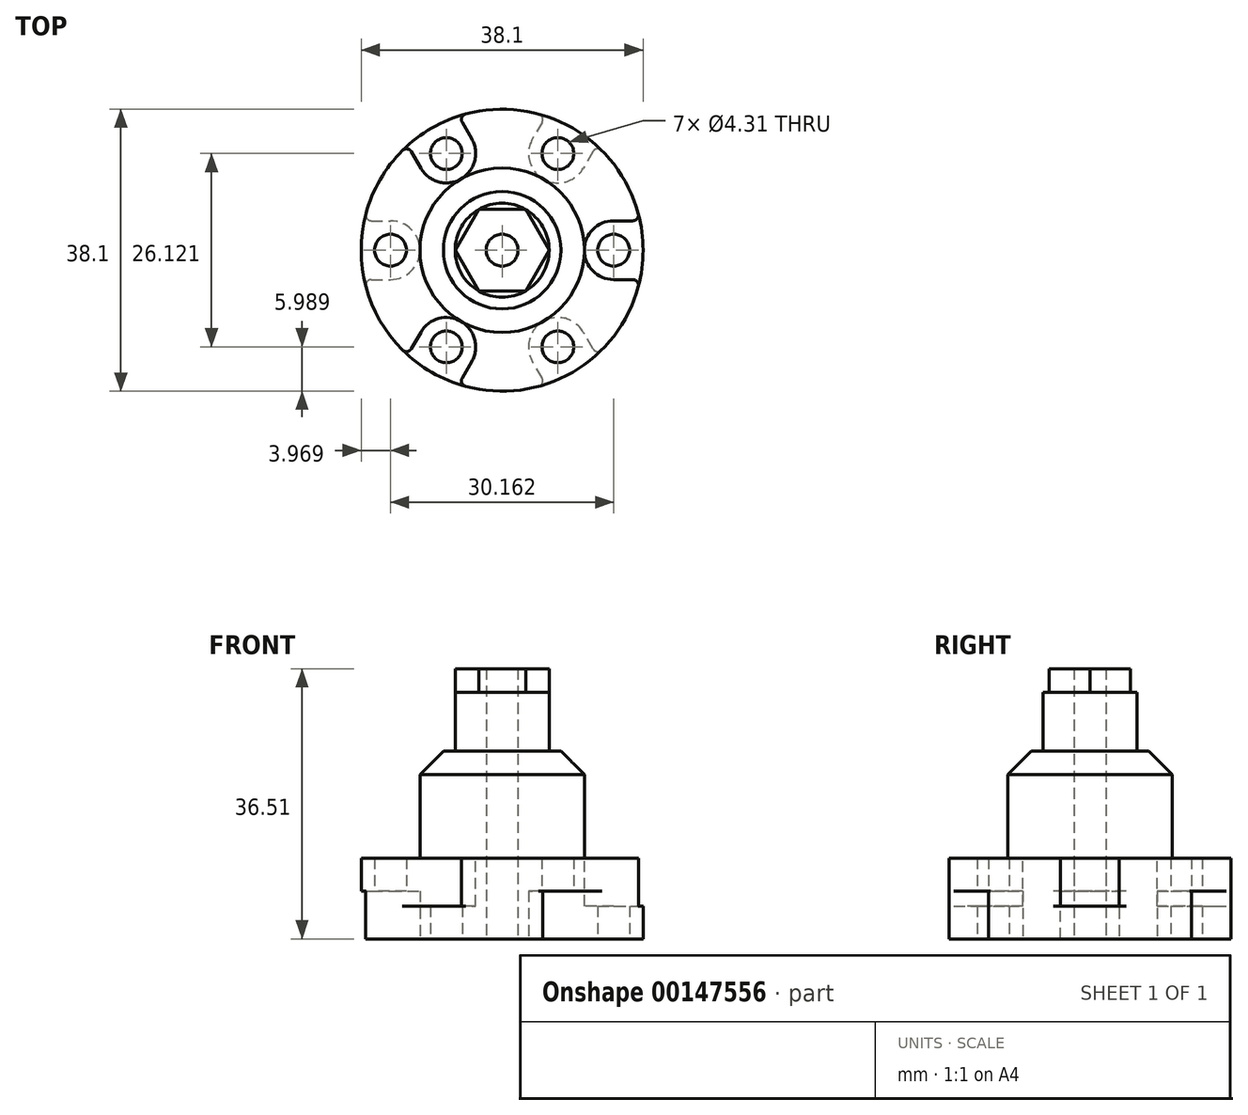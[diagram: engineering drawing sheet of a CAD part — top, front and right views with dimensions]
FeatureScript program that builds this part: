
annotation { "Feature Type Name" : "Feature", "Feature Type Description" : "" }
export const myFeature = defineFeature(function(context is Context, id is Id, definition is map)
    precondition{}
    {
        {
            var Q0;
            Q0=qCreatedBy(makeId("Top.planeOp"),FACE);
            var sketch = newSketch(context, id + "F0", { "sketchPlane" : qUnion([Q0])});
            skCircle(sketch, "E0", {"center": v(0, 0) * mm, "radius": 19.05 * mm});
            skCircle(sketch, "E1", {"center": v(7.54, -13.06) * mm, "radius": 3.97 * mm, "construction": true});
            skCircle(sketch, "E2", {"center": v(0, 0) * mm, "radius": 11.11 * mm, "construction": true});
            skCircle(sketch, "E3.cCircle", {"center": v(0, 0) * mm, "radius": 13.06 * mm, "construction": true});
            skLineSegment(sketch, "E3.0", {"start": v(-7.54, 13.06) * mm, "end": v(7.54, 13.06) * mm, "construction": true});
            skLineSegment(sketch, "E3.1", {"start": v(7.54, 13.06) * mm, "end": v(15.08, 0) * mm, "construction": true});
            skLineSegment(sketch, "E3.2", {"start": v(15.08, 0) * mm, "end": v(7.54, -13.06) * mm, "construction": true});
            skLineSegment(sketch, "E3.3", {"start": v(7.54, -13.06) * mm, "end": v(-7.54, -13.06) * mm, "construction": true});
            skLineSegment(sketch, "E3.4", {"start": v(-7.54, -13.06) * mm, "end": v(-15.08, 0) * mm, "construction": true});
            skLineSegment(sketch, "E3.5", {"start": v(-15.08, 0) * mm, "end": v(-7.54, 13.06) * mm, "construction": true});
            skPoint(sketch, "E3.0.midPoint", {"position": v(0, 13.06) * mm});
            skCircle(sketch, "E4", {"center": v(-7.54, -13.06) * mm, "radius": 2.15 * mm});
            skCircle(sketch, "E5", {"center": v(-15.08, 0) * mm, "radius": 2.15 * mm});
            skCircle(sketch, "E6", {"center": v(-7.54, 13.06) * mm, "radius": 2.15 * mm});
            skCircle(sketch, "E7", {"center": v(7.54, 13.06) * mm, "radius": 2.15 * mm});
            skCircle(sketch, "E8", {"center": v(15.08, 0) * mm, "radius": 2.15 * mm});
            skCircle(sketch, "E9", {"center": v(7.54, -13.06) * mm, "radius": 2.15 * mm});
            skCircle(sketch, "E10", {"center": v(0, 0) * mm, "radius": 2.15 * mm});
            skSolve(sketch);
        }
        {
            var Q0;
            Q0=qSketchRegion(id+"F0",true);
            extrude(context, id + "F1", {"entities" : qUnion([Q0]), "depth" : 10.92 * mm});
        }
        {
            var Q0;
            Q0=makeQuery(id+"F1.opExtrude","CAP_FACE",FACE,{"disambiguationData":[OSD([sQuery(id+"F0.wireOp",EDGE,"E0"),sQuery(id+"F0.wireOp",EDGE,"E4"),sQuery(id+"F0.wireOp",EDGE,"E5"),sQuery(id+"F0.wireOp",EDGE,"E6"),sQuery(id+"F0.wireOp",EDGE,"E7"),sQuery(id+"F0.wireOp",EDGE,"E8"),sQuery(id+"F0.wireOp",EDGE,"E9")])],"isStart":false});
            cPlane(context, id + "F2", {"entities" : qUnion([Q0]), "cplaneType" : CPlaneType.OFFSET, "offset" : 4.44 * mm, "oppositeDirection" : true, "width" : 152.4 * mm, "height" : 152.4 * mm});
        }
        {
            var Q0;
            Q0=makeQuery(id+"F1.opExtrude","CAP_FACE",FACE,{"disambiguationData":[OSD([sQuery(id+"F0.wireOp",EDGE,"E0"),sQuery(id+"F0.wireOp",EDGE,"E4"),sQuery(id+"F0.wireOp",EDGE,"E5"),sQuery(id+"F0.wireOp",EDGE,"E6"),sQuery(id+"F0.wireOp",EDGE,"E7"),sQuery(id+"F0.wireOp",EDGE,"E8"),sQuery(id+"F0.wireOp",EDGE,"E9")])],"isStart":true});
            cPlane(context, id + "F3", {"entities" : qUnion([Q0]), "cplaneType" : CPlaneType.OFFSET, "offset" : 4.44 * mm, "oppositeDirection" : true, "width" : 152.4 * mm, "height" : 152.4 * mm});
        }
        {
            var Q0;
            Q0=makeQuery(id+"F1.opExtrude","CAP_FACE",FACE,{"disambiguationData":[OSD([sQuery(id+"F0.wireOp",EDGE,"E0"),sQuery(id+"F0.wireOp",EDGE,"E4"),sQuery(id+"F0.wireOp",EDGE,"E5"),sQuery(id+"F0.wireOp",EDGE,"E6"),sQuery(id+"F0.wireOp",EDGE,"E7"),sQuery(id+"F0.wireOp",EDGE,"E8"),sQuery(id+"F0.wireOp",EDGE,"E9")])],"isStart":false});
            var sketch = newSketch(context, id + "F4", { "sketchPlane" : qUnion([Q0])});
            skLineSegment(sketch, "E11", {"start": v(-7.54, 13.06) * mm, "end": v(0, 0) * mm, "construction": true});
            skLineSegment(sketch, "E12", {"start": v(15.08, 0) * mm, "end": v(0, 0) * mm, "construction": true});
            skLineSegment(sketch, "E13", {"start": v(0, 0) * mm, "end": v(-7.54, -13.06) * mm, "construction": true});
            skLineSegment(sketch, "E14.bottom", {"start": v(-10.98, 11.08) * mm, "end": v(-4.1, 15.05) * mm, "construction": true});
            skLineSegment(sketch, "E14.top", {"start": v(-12.96, 14.51) * mm, "end": v(-6.09, 18.48) * mm});
            skLineSegment(sketch, "E14.left", {"start": v(-10.98, 11.08) * mm, "end": v(-12.96, 14.51) * mm});
            skLineSegment(sketch, "E14.right", {"start": v(-4.1, 15.05) * mm, "end": v(-6.09, 18.48) * mm});
            skLineSegment(sketch, "E15.bottom", {"start": v(15.08, 3.97) * mm, "end": v(19.05, 3.97) * mm});
            skLineSegment(sketch, "E15.top", {"start": v(15.08, -3.97) * mm, "end": v(19.05, -3.97) * mm});
            skLineSegment(sketch, "E15.left", {"start": v(15.08, 3.97) * mm, "end": v(15.08, -3.97) * mm, "construction": true});
            skLineSegment(sketch, "E15.right", {"start": v(19.05, 3.97) * mm, "end": v(19.05, -3.97) * mm});
            skLineSegment(sketch, "E16.bottom", {"start": v(-10.98, -11.08) * mm, "end": v(-4.1, -15.05) * mm, "construction": true});
            skLineSegment(sketch, "E16.top", {"start": v(-12.96, -14.51) * mm, "end": v(-6.09, -18.48) * mm});
            skLineSegment(sketch, "E16.left", {"start": v(-10.98, -11.08) * mm, "end": v(-12.96, -14.51) * mm});
            skLineSegment(sketch, "E16.right", {"start": v(-4.1, -15.05) * mm, "end": v(-6.09, -18.48) * mm});
            skArc(sketch, "E17", {"start": v(-4.1, -15.05) * mm, "mid": v(-5.56, -9.62) * mm, "end": v(-10.98, -11.08) * mm});
            skArc(sketch, "E18", {"start": v(15.08, 3.97) * mm, "mid": v(11.11, 0) * mm, "end": v(15.08, -3.97) * mm});
            skArc(sketch, "E19", {"start": v(-10.98, 11.08) * mm, "mid": v(-5.56, 9.62) * mm, "end": v(-4.1, 15.05) * mm});
            skSolve(sketch);
        }
        {
            var Q0;
            Q0=qSketchRegion(id+"F4",true);
            var Q1;
            Q1=qCreatedBy(id+"F3.planeOp",FACE);
            extrude(context, id + "F5", {"entities" : qUnion([Q0]), "operationType" : NewBodyOperationType.REMOVE, "endBound" : BoundingType.UP_TO_SURFACE, "oppositeDirection" : true, "endBoundEntityFace" : qUnion([Q1]), "depth" : 25.4 * mm});
        }
        {
            var Q0;
            Q0=makeQuery(id+"F1.opExtrude","CAP_FACE",FACE,{"disambiguationData":[OSD([sQuery(id+"F0.wireOp",EDGE,"E0"),sQuery(id+"F0.wireOp",EDGE,"E4"),sQuery(id+"F0.wireOp",EDGE,"E5"),sQuery(id+"F0.wireOp",EDGE,"E6"),sQuery(id+"F0.wireOp",EDGE,"E7"),sQuery(id+"F0.wireOp",EDGE,"E8"),sQuery(id+"F0.wireOp",EDGE,"E9"),sQuery(id+"F0.wireOp",EDGE,"E10")])],"isStart":true});
            var sketch = newSketch(context, id + "F6", { "sketchPlane" : qUnion([Q0])});
            skLineSegment(sketch, "E20", {"start": v(0, 0) * mm, "end": v(-15.08, 0) * mm, "construction": true});
            skLineSegment(sketch, "E21", {"start": v(0, 0) * mm, "end": v(7.54, 13.06) * mm, "construction": true});
            skLineSegment(sketch, "E22", {"start": v(0, 0) * mm, "end": v(7.54, -13.06) * mm, "construction": true});
            skLineSegment(sketch, "E23.bottom", {"start": v(6.09, -18.48) * mm, "end": v(12.96, -14.51) * mm});
            skLineSegment(sketch, "E23.top", {"start": v(4.1, -15.05) * mm, "end": v(10.98, -11.08) * mm, "construction": true});
            skLineSegment(sketch, "E23.left", {"start": v(6.09, -18.48) * mm, "end": v(4.1, -15.05) * mm});
            skLineSegment(sketch, "E23.right", {"start": v(12.96, -14.51) * mm, "end": v(10.98, -11.08) * mm});
            skLineSegment(sketch, "E24.bottom", {"start": v(6.09, 18.48) * mm, "end": v(12.96, 14.51) * mm});
            skLineSegment(sketch, "E24.top", {"start": v(4.1, 15.05) * mm, "end": v(10.98, 11.08) * mm, "construction": true});
            skLineSegment(sketch, "E24.left", {"start": v(6.09, 18.48) * mm, "end": v(4.1, 15.05) * mm});
            skLineSegment(sketch, "E24.right", {"start": v(12.96, 14.51) * mm, "end": v(10.98, 11.08) * mm});
            skLineSegment(sketch, "E25.bottom", {"start": v(-19.05, 3.97) * mm, "end": v(-15.08, 3.97) * mm});
            skLineSegment(sketch, "E25.top", {"start": v(-19.05, -3.97) * mm, "end": v(-15.08, -3.97) * mm});
            skLineSegment(sketch, "E25.left", {"start": v(-19.05, 3.97) * mm, "end": v(-19.05, -3.97) * mm});
            skLineSegment(sketch, "E25.right", {"start": v(-15.08, 3.97) * mm, "end": v(-15.08, -3.97) * mm, "construction": true});
            skArc(sketch, "E26", {"start": v(10.98, -11.08) * mm, "mid": v(5.56, -9.62) * mm, "end": v(4.1, -15.05) * mm});
            skArc(sketch, "E27", {"start": v(4.1, 15.05) * mm, "mid": v(5.56, 9.62) * mm, "end": v(10.98, 11.08) * mm});
            skArc(sketch, "E28", {"start": v(-15.08, -3.97) * mm, "mid": v(-11.11, 0) * mm, "end": v(-15.08, 3.97) * mm});
            skSolve(sketch);
        }
        {
            var Q0;
            Q0=qSketchRegion(id+"F6",true);
            var Q1;
            Q1=qCreatedBy(id+"F2.planeOp",FACE);
            extrude(context, id + "F7", {"entities" : qUnion([Q0]), "operationType" : NewBodyOperationType.REMOVE, "endBound" : BoundingType.UP_TO_SURFACE, "oppositeDirection" : true, "endBoundEntityFace" : qUnion([Q1]), "depth" : 25.4 * mm});
        }
        {
            var Q0;
            Q0=makeQuery(id+"F1.opExtrude","CAP_FACE",FACE,{"disambiguationData":[OSD([sQuery(id+"F0.wireOp",EDGE,"E0"),sQuery(id+"F0.wireOp",EDGE,"E4"),sQuery(id+"F0.wireOp",EDGE,"E5"),sQuery(id+"F0.wireOp",EDGE,"E6"),sQuery(id+"F0.wireOp",EDGE,"E7"),sQuery(id+"F0.wireOp",EDGE,"E8"),sQuery(id+"F0.wireOp",EDGE,"E9"),sQuery(id+"F0.wireOp",EDGE,"E10")])],"isStart":false});
            var sketch = newSketch(context, id + "F8", { "sketchPlane" : qUnion([Q0])});
            skCircle(sketch, "E29", {"center": v(0, 0) * mm, "radius": 11.11 * mm});
            skCircle(sketch, "E30", {"center": v(0, 0) * mm, "radius": 2.15 * mm});
            skSolve(sketch);
        }
        {
            var Q0;
            Q0=qSketchRegion(id+"F8",true);
            extrude(context, id + "F9", {"entities" : qUnion([Q0]), "operationType" : NewBodyOperationType.ADD, "depth" : 14.48 * mm});
        }
        {
            var Q0;
            Q0=makeQuery(id+"F9.opExtrude","CAP_FACE",FACE,{"disambiguationData":[OSD([sQuery(id+"F8.wireOp",EDGE,"E29"),sQuery(id+"F8.wireOp",EDGE,"E30")])],"isStart":false});
            var sketch = newSketch(context, id + "F10", { "sketchPlane" : qUnion([Q0])});
            skCircle(sketch, "E31", {"center": v(0, 0) * mm, "radius": 6.35 * mm});
            skCircle(sketch, "E32", {"center": v(0, 0) * mm, "radius": 2.15 * mm});
            skSolve(sketch);
        }
        {
            var Q0;
            Q0=qSketchRegion(id+"F10",true);
            extrude(context, id + "F11", {"entities" : qUnion([Q0]), "operationType" : NewBodyOperationType.ADD, "depth" : 7.94 * mm});
        }
        {
            var Q0;
            Q0=makeQuery(id+"F11.opExtrude","CAP_FACE",FACE,{"disambiguationData":[OSD([sQuery(id+"F10.wireOp",EDGE,"E31"),sQuery(id+"F10.wireOp",EDGE,"E32")])],"isStart":false});
            var sketch = newSketch(context, id + "F12", { "sketchPlane" : qUnion([Q0])});
            skCircle(sketch, "E33.cCircle", {"center": v(0, 0) * mm, "radius": 6.35 * mm, "construction": true});
            skLineSegment(sketch, "E33.0", {"start": v(-3.18, 5.5) * mm, "end": v(3.17, 5.5) * mm});
            skLineSegment(sketch, "E33.1", {"start": v(3.17, 5.5) * mm, "end": v(6.35, 0) * mm});
            skLineSegment(sketch, "E33.2", {"start": v(6.35, 0) * mm, "end": v(3.18, -5.5) * mm});
            skLineSegment(sketch, "E33.3", {"start": v(3.18, -5.5) * mm, "end": v(-3.17, -5.5) * mm});
            skLineSegment(sketch, "E33.4", {"start": v(-3.17, -5.5) * mm, "end": v(-6.35, 0) * mm});
            skLineSegment(sketch, "E33.5", {"start": v(-6.35, 0) * mm, "end": v(-3.18, 5.5) * mm});
            skCircle(sketch, "E34", {"center": v(0, 0) * mm, "radius": 2.15 * mm});
            skSolve(sketch);
        }
        {
            var Q0;
            Q0=qSketchRegion(id+"F12",true);
            extrude(context, id + "F13", {"entities" : qUnion([Q0]), "operationType" : NewBodyOperationType.ADD, "depth" : 3.17 * mm});
        }
        {
            var Q0;
            Q0=makeQuery(id+"F5.boolean.opBoolean","INTERSECT",EDGE,{"derivedFrom":[makeQuery(id+"F1.opExtrude","SWEPT_FACE",FACE,{"disambiguationData":[OSD([sQuery(id+"F0.wireOp",EDGE,"E0")])]}),makeQuery(id+"F5.opExtrude","SWEPT_FACE",FACE,{"disambiguationData":[OSD([sQuery(id+"F4.wireOp",EDGE,"E16.left")])]})]});
            var Q1;
            Q1=makeQuery(id+"F7.boolean.opBoolean","INTERSECT",EDGE,{"derivedFrom":[makeQuery(id+"F1.opExtrude","SWEPT_FACE",FACE,{"disambiguationData":[OSD([sQuery(id+"F0.wireOp",EDGE,"E0")])]}),makeQuery(id+"F7.opExtrude","SWEPT_FACE",FACE,{"disambiguationData":[OSD([sQuery(id+"F6.wireOp",EDGE,"E24.left")])]})]});
            var Q2;
            Q2=makeQuery(id+"F7.boolean.opBoolean","INTERSECT",EDGE,{"derivedFrom":[makeQuery(id+"F1.opExtrude","SWEPT_FACE",FACE,{"disambiguationData":[OSD([sQuery(id+"F0.wireOp",EDGE,"E0")])]}),makeQuery(id+"F7.opExtrude","SWEPT_FACE",FACE,{"disambiguationData":[OSD([sQuery(id+"F6.wireOp",EDGE,"E24.right")])]})]});
            var Q3;
            Q3=makeQuery(id+"F5.boolean.opBoolean","INTERSECT",EDGE,{"derivedFrom":[makeQuery(id+"F1.opExtrude","SWEPT_FACE",FACE,{"disambiguationData":[OSD([sQuery(id+"F0.wireOp",EDGE,"E0")])]}),makeQuery(id+"F5.opExtrude","SWEPT_FACE",FACE,{"disambiguationData":[OSD([sQuery(id+"F4.wireOp",EDGE,"E15.bottom")])]})]});
            var Q4;
            Q4=makeQuery(id+"F5.boolean.opBoolean","INTERSECT",EDGE,{"derivedFrom":[makeQuery(id+"F1.opExtrude","SWEPT_FACE",FACE,{"disambiguationData":[OSD([sQuery(id+"F0.wireOp",EDGE,"E0")])]}),makeQuery(id+"F5.opExtrude","SWEPT_FACE",FACE,{"disambiguationData":[OSD([sQuery(id+"F4.wireOp",EDGE,"E15.top")])]})]});
            var Q5;
            Q5=makeQuery(id+"F5.boolean.opBoolean","INTERSECT",EDGE,{"derivedFrom":[makeQuery(id+"F1.opExtrude","SWEPT_FACE",FACE,{"disambiguationData":[OSD([sQuery(id+"F0.wireOp",EDGE,"E0")])]}),makeQuery(id+"F5.opExtrude","SWEPT_FACE",FACE,{"disambiguationData":[OSD([sQuery(id+"F4.wireOp",EDGE,"E16.right")])]})]});
            var Q6;
            Q6=makeQuery(id+"F7.boolean.opBoolean","INTERSECT",EDGE,{"derivedFrom":[makeQuery(id+"F1.opExtrude","SWEPT_FACE",FACE,{"disambiguationData":[OSD([sQuery(id+"F0.wireOp",EDGE,"E0")])]}),makeQuery(id+"F7.opExtrude","SWEPT_FACE",FACE,{"disambiguationData":[OSD([sQuery(id+"F6.wireOp",EDGE,"E23.right")])]})]});
            var Q7;
            Q7=makeQuery(id+"F7.boolean.opBoolean","INTERSECT",EDGE,{"derivedFrom":[makeQuery(id+"F1.opExtrude","SWEPT_FACE",FACE,{"disambiguationData":[OSD([sQuery(id+"F0.wireOp",EDGE,"E0")])]}),makeQuery(id+"F7.opExtrude","SWEPT_FACE",FACE,{"disambiguationData":[OSD([sQuery(id+"F6.wireOp",EDGE,"E23.left")])]})]});
            var Q8;
            Q8=makeQuery(id+"F5.boolean.opBoolean","INTERSECT",EDGE,{"derivedFrom":[makeQuery(id+"F1.opExtrude","SWEPT_FACE",FACE,{"disambiguationData":[OSD([sQuery(id+"F0.wireOp",EDGE,"E0")])]}),makeQuery(id+"F5.opExtrude","SWEPT_FACE",FACE,{"disambiguationData":[OSD([sQuery(id+"F4.wireOp",EDGE,"E14.right")])]})]});
            var Q9;
            Q9=makeQuery(id+"F5.boolean.opBoolean","INTERSECT",EDGE,{"derivedFrom":[makeQuery(id+"F1.opExtrude","SWEPT_FACE",FACE,{"disambiguationData":[OSD([sQuery(id+"F0.wireOp",EDGE,"E0")])]}),makeQuery(id+"F5.opExtrude","SWEPT_FACE",FACE,{"disambiguationData":[OSD([sQuery(id+"F4.wireOp",EDGE,"E14.left")])]})]});
            var Q10;
            Q10=makeQuery(id+"F7.boolean.opBoolean","INTERSECT",EDGE,{"derivedFrom":[makeQuery(id+"F1.opExtrude","SWEPT_FACE",FACE,{"disambiguationData":[OSD([sQuery(id+"F0.wireOp",EDGE,"E0")])]}),makeQuery(id+"F7.opExtrude","SWEPT_FACE",FACE,{"disambiguationData":[OSD([sQuery(id+"F6.wireOp",EDGE,"E25.top")])]})]});
            var Q11;
            Q11=makeQuery(id+"F7.boolean.opBoolean","INTERSECT",EDGE,{"derivedFrom":[makeQuery(id+"F1.opExtrude","SWEPT_FACE",FACE,{"disambiguationData":[OSD([sQuery(id+"F0.wireOp",EDGE,"E0")])]}),makeQuery(id+"F7.opExtrude","SWEPT_FACE",FACE,{"disambiguationData":[OSD([sQuery(id+"F6.wireOp",EDGE,"E25.bottom")])]})]});
            fillet(context, id + "F14", {"entities" : qUnion([Q0, Q1, Q2, Q3, Q4, Q5, Q6, Q7, Q8, Q9, Q10, Q11]), "radius" : 0.76 * mm, "tangentPropagation" : true, "allowEdgeOverflow" : false});
        }
        {
            var Q0;
            Q0=makeQuery(id+"F9.opExtrude","CAP_EDGE",EDGE,{"disambiguationData":[OSD([sQuery(id+"F8.wireOp",EDGE,"E29")])],"isStart":false});
            chamfer(context, id + "F15", {"entities" : qUnion([Q0]), "width" : 3.17 * mm, "tangentPropagation" : true});
        }
    });
